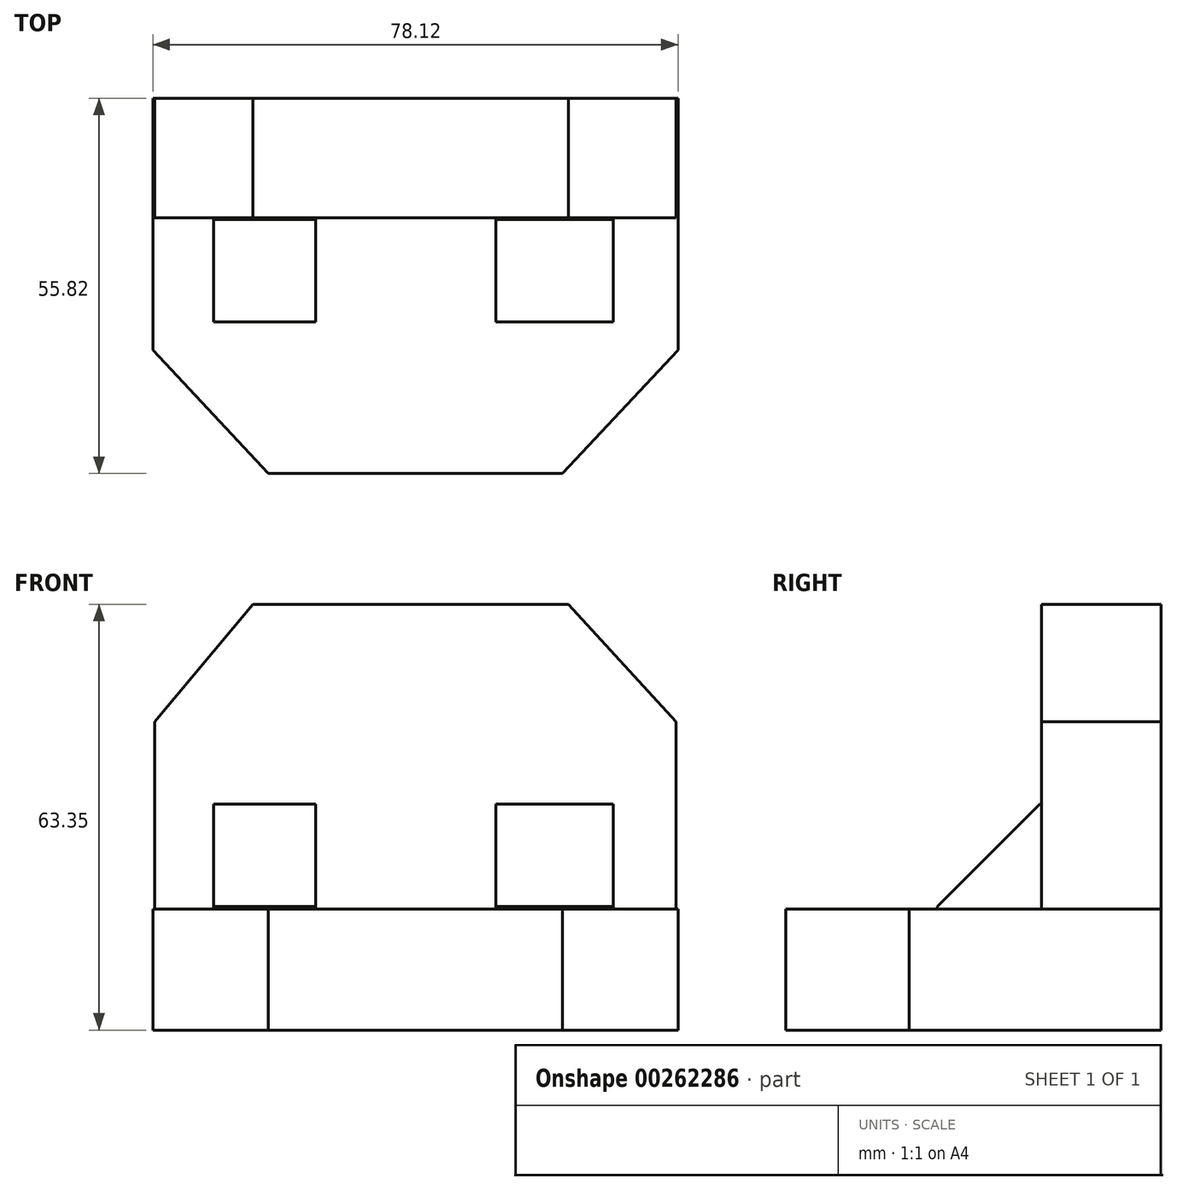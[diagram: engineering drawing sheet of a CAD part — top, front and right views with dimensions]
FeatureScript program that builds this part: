
annotation { "Feature Type Name" : "Feature", "Feature Type Description" : "" }
export const myFeature = defineFeature(function(context is Context, id is Id, definition is map)
    precondition{}
    {
        {
            var Q0;
            Q0=qCreatedBy(makeId("Front.planeOp"),FACE);
            var sketch = newSketch(context, id + "F0", { "sketchPlane" : qUnion([Q0])});
            skLineSegment(sketch, "E0.bottom", {"start": v(-35.27, 0) * mm, "end": v(42.26, 0) * mm});
            skLineSegment(sketch, "E0.top", {"start": v(-35.27, 27.84) * mm, "end": v(42.26, 27.84) * mm});
            skLineSegment(sketch, "E0.left", {"start": v(-35.27, 0) * mm, "end": v(-35.27, 27.84) * mm});
            skLineSegment(sketch, "E0.right", {"start": v(42.26, 0) * mm, "end": v(42.26, 27.84) * mm});
            skLineSegment(sketch, "E1", {"start": v(-35.27, 27.84) * mm, "end": v(-20.7, 45.32) * mm});
            skLineSegment(sketch, "E2", {"start": v(42.26, 27.84) * mm, "end": v(26.23, 45.32) * mm});
            skLineSegment(sketch, "E3", {"start": v(26.23, 45.32) * mm, "end": v(-20.7, 45.32) * mm});
            skSolve(sketch);
        }
        {
            var Q0;
            Q0 = qSketchRegion(id + "F0", true);
            extrude(context, id + "F1", {"entities" : qUnion([Q0]), "depth" : 17.78 * mm});
        }
        {
            var Q0;
            Q0=qCreatedBy(makeId("Top.planeOp"),FACE);
            var sketch = newSketch(context, id + "F2", { "sketchPlane" : qUnion([Q0])});
            skLineSegment(sketch, "E4.bottom", {"start": v(42.56, 0) * mm, "end": v(-35.56, 0) * mm});
            skLineSegment(sketch, "E4.top", {"start": v(42.56, -37.45) * mm, "end": v(-35.56, -37.45) * mm});
            skLineSegment(sketch, "E4.left", {"start": v(42.56, 0) * mm, "end": v(42.56, -37.45) * mm});
            skLineSegment(sketch, "E4.right", {"start": v(-35.56, 0) * mm, "end": v(-35.56, -37.45) * mm});
            skLineSegment(sketch, "E5", {"start": v(42.56, -37.45) * mm, "end": v(25.36, -55.82) * mm});
            skLineSegment(sketch, "E6", {"start": v(-35.56, -37.45) * mm, "end": v(-18.36, -55.82) * mm});
            skLineSegment(sketch, "E7", {"start": v(-18.36, -55.82) * mm, "end": v(25.36, -55.82) * mm});
            skSolve(sketch);
        }
        {
            var Q0;
            Q0 = qSketchRegion(id + "F2", true);
            extrude(context, id + "F3", {"entities" : qUnion([Q0]), "operationType" : NewBodyOperationType.ADD, "oppositeDirection" : true, "depth" : 18.03 * mm});
        }
        {
            var Q0;
            Q0=makeQuery(id+"F1.opExtrude","CAP_FACE",FACE,{"disambiguationData":[OSD([sQuery(id+"F0.wireOp",EDGE,"E0.bottom"),sQuery(id+"F0.wireOp",EDGE,"E0.left"),sQuery(id+"F0.wireOp",EDGE,"E0.right"),sQuery(id+"F0.wireOp",EDGE,"E1"),sQuery(id+"F0.wireOp",EDGE,"E2"),sQuery(id+"F0.wireOp",EDGE,"E3")])],"isStart":false});
            var sketch = newSketch(context, id + "F4", { "sketchPlane" : qUnion([Q0])});
            skLineSegment(sketch, "E8.bottom", {"start": v(-26.52, 0) * mm, "end": v(-11.37, 0) * mm});
            skLineSegment(sketch, "E8.top", {"start": v(-26.52, 15.6) * mm, "end": v(-11.37, 15.6) * mm});
            skLineSegment(sketch, "E8.left", {"start": v(-26.52, 0) * mm, "end": v(-26.52, 15.6) * mm});
            skLineSegment(sketch, "E8.right", {"start": v(-11.37, 0) * mm, "end": v(-11.37, 15.6) * mm});
            skLineSegment(sketch, "E9.bottom", {"start": v(15.45, 0) * mm, "end": v(32.94, 0) * mm});
            skLineSegment(sketch, "E9.top", {"start": v(15.45, 15.6) * mm, "end": v(32.94, 15.6) * mm});
            skLineSegment(sketch, "E9.left", {"start": v(15.45, 0) * mm, "end": v(15.45, 15.6) * mm});
            skLineSegment(sketch, "E9.right", {"start": v(32.94, 0) * mm, "end": v(32.94, 15.6) * mm});
            skSolve(sketch);
        }
        {
            var Q0;
            Q0 = qSketchRegion(id + "F4", true);
            extrude(context, id + "F5", {"entities" : qUnion([Q0]), "operationType" : NewBodyOperationType.ADD, "depth" : 15.5 * mm});
        }
        {
            var Q0;
            Q0=makeQuery(id+"F5.opExtrude","CAP_EDGE",EDGE,{"disambiguationData":[OSD([sQuery(id+"F4.wireOp",EDGE,"E8.top")])],"isStart":false});
            var Q1;
            Q1=makeQuery(id+"F5.opExtrude","CAP_EDGE",EDGE,{"disambiguationData":[OSD([sQuery(id+"F4.wireOp",EDGE,"E9.top")])],"isStart":false});
            chamfer(context, id + "F6", {"entities" : qUnion([Q0, Q1]), "width" : 15.24 * mm, "tangentPropagation" : true});
        }
    });
